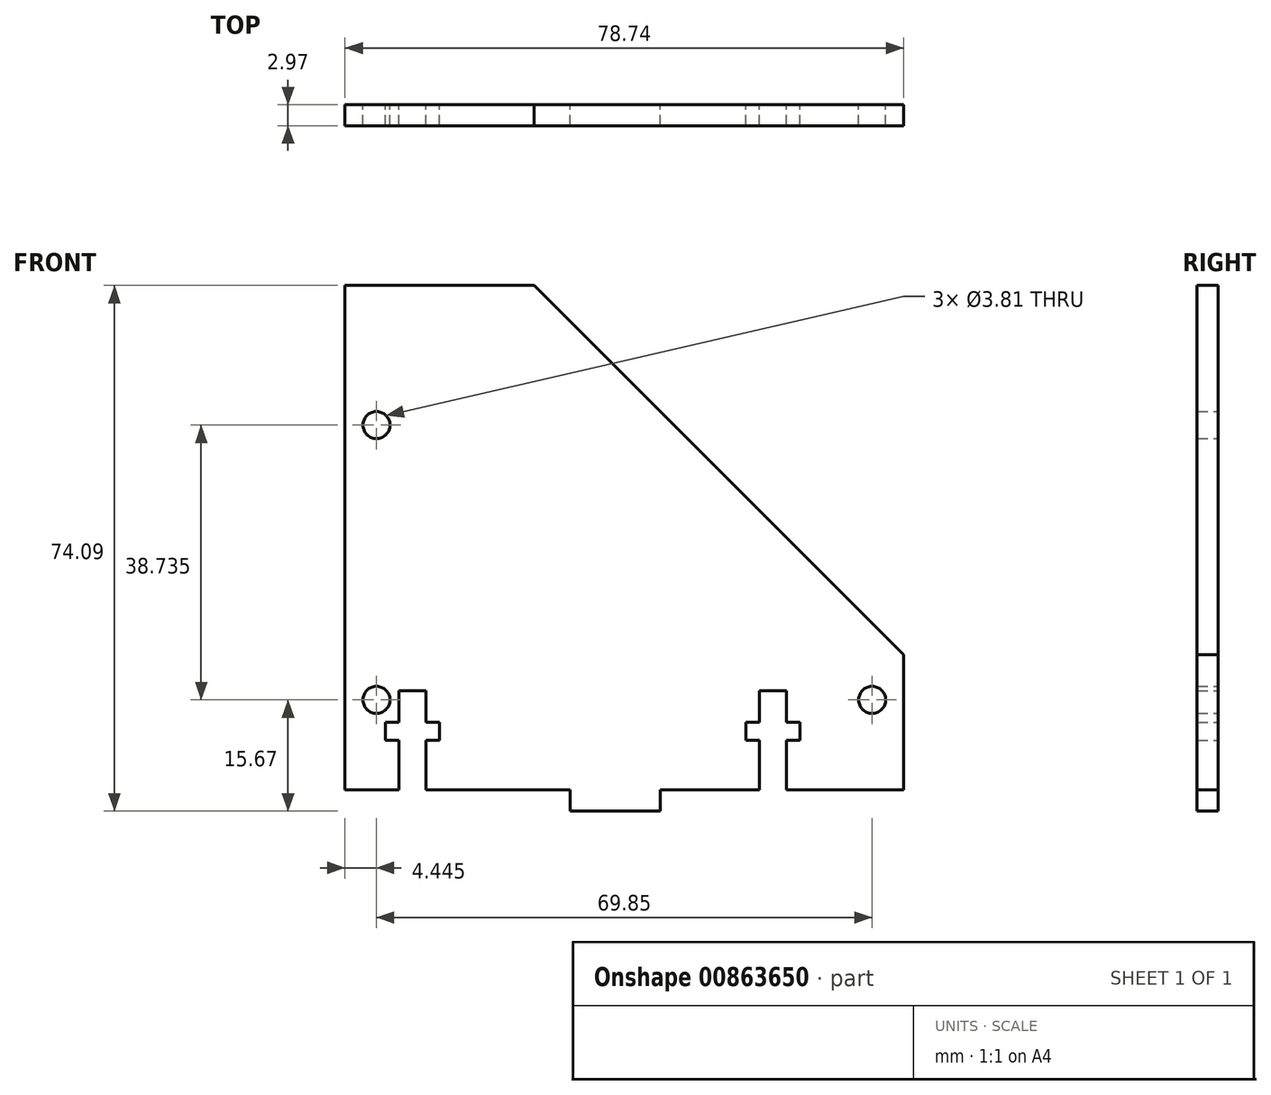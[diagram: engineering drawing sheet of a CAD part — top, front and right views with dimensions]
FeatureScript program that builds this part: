
annotation { "Feature Type Name" : "Feature", "Feature Type Description" : "" }
export const myFeature = defineFeature(function(context is Context, id is Id, definition is map)
    precondition{}
    {
        {
            var Q0;
            Q0=qCreatedBy(makeId("Front.planeOp"),FACE);
            var sketch = newSketch(context, id + "F0", { "sketchPlane" : qUnion([Q0])});
            skLineSegment(sketch, "E0", {"start": v(0, 0) * mm, "end": v(0, 71.12) * mm});
            skLineSegment(sketch, "E1", {"start": v(0, 71.12) * mm, "end": v(26.67, 71.12) * mm});
            skLineSegment(sketch, "E2", {"start": v(26.67, 71.12) * mm, "end": v(78.74, 19.05) * mm});
            skLineSegment(sketch, "E3", {"start": v(78.74, 19.05) * mm, "end": v(78.74, 0) * mm});
            skLineSegment(sketch, "E4", {"start": v(78.74, 0) * mm, "end": v(62.23, 0) * mm});
            skLineSegment(sketch, "E5", {"start": v(44.45, 0) * mm, "end": v(44.45, -2.97) * mm});
            skLineSegment(sketch, "E6", {"start": v(44.45, -2.97) * mm, "end": v(31.75, -2.97) * mm});
            skLineSegment(sketch, "E7", {"start": v(31.75, -2.97) * mm, "end": v(31.75, 0) * mm});
            skLineSegment(sketch, "E8", {"start": v(31.75, 0) * mm, "end": v(11.43, 0) * mm});
            skCircle(sketch, "E9", {"center": v(4.44, 51.44) * mm, "radius": 1.9 * mm});
            skCircle(sketch, "E10", {"center": v(4.45, 12.7) * mm, "radius": 1.9 * mm});
            skLineSegment(sketch, "E11", {"start": v(7.62, 0) * mm, "end": v(7.62, 6.99) * mm});
            skLineSegment(sketch, "E12", {"start": v(7.62, 6.99) * mm, "end": v(5.72, 6.99) * mm});
            skLineSegment(sketch, "E13", {"start": v(5.72, 6.99) * mm, "end": v(5.72, 9.53) * mm});
            skLineSegment(sketch, "E14", {"start": v(5.72, 9.53) * mm, "end": v(7.62, 9.53) * mm});
            skLineSegment(sketch, "E15", {"start": v(7.62, 9.53) * mm, "end": v(7.62, 13.97) * mm});
            skLineSegment(sketch, "E16", {"start": v(7.62, 13.97) * mm, "end": v(11.43, 13.97) * mm});
            skLineSegment(sketch, "E17", {"start": v(11.43, 13.97) * mm, "end": v(11.43, 9.53) * mm});
            skLineSegment(sketch, "E18", {"start": v(11.43, 9.53) * mm, "end": v(13.34, 9.53) * mm});
            skLineSegment(sketch, "E19", {"start": v(13.34, 9.53) * mm, "end": v(13.34, 6.99) * mm});
            skLineSegment(sketch, "E20", {"start": v(13.34, 6.99) * mm, "end": v(11.43, 6.99) * mm});
            skLineSegment(sketch, "E21", {"start": v(11.43, 6.99) * mm, "end": v(11.43, 0) * mm});
            skLineSegment(sketch, "E22.trimOffspring", {"start": v(7.62, 0) * mm, "end": v(0, 0) * mm});
            skCircle(sketch, "E23", {"center": v(74.3, 12.7) * mm, "radius": 1.9 * mm});
            skLineSegment(sketch, "E24", {"start": v(38.1, -2.97) * mm, "end": v(38.1, 59.69) * mm, "construction": true});
            skLineSegment(sketch, "E25.1.0.0", {"start": v(58.42, 0) * mm, "end": v(58.42, 6.99) * mm});
            skLineSegment(sketch, "E25.1.0.1", {"start": v(58.42, 6.99) * mm, "end": v(56.52, 6.99) * mm});
            skLineSegment(sketch, "E25.1.0.2", {"start": v(56.52, 6.99) * mm, "end": v(56.52, 9.53) * mm});
            skLineSegment(sketch, "E25.1.0.3", {"start": v(56.52, 9.53) * mm, "end": v(58.42, 9.53) * mm});
            skLineSegment(sketch, "E25.1.0.4", {"start": v(58.42, 9.53) * mm, "end": v(58.42, 13.97) * mm});
            skLineSegment(sketch, "E25.1.0.5", {"start": v(58.42, 13.97) * mm, "end": v(62.23, 13.97) * mm});
            skLineSegment(sketch, "E25.1.0.6", {"start": v(62.23, 13.97) * mm, "end": v(62.23, 9.53) * mm});
            skLineSegment(sketch, "E25.1.0.7", {"start": v(62.23, 9.53) * mm, "end": v(64.14, 9.53) * mm});
            skLineSegment(sketch, "E25.1.0.8", {"start": v(64.14, 6.99) * mm, "end": v(62.23, 6.99) * mm});
            skLineSegment(sketch, "E25.1.0.9", {"start": v(64.14, 9.53) * mm, "end": v(64.14, 6.99) * mm});
            skLineSegment(sketch, "E25.1.0.10", {"start": v(62.23, 6.99) * mm, "end": v(62.23, 0) * mm});
            skLineSegment(sketch, "E25.direction1", {"start": v(7.62, 0) * mm, "end": v(58.42, 0) * mm, "construction": true});
            skLineSegment(sketch, "E26.trimOffspring", {"start": v(58.42, 0) * mm, "end": v(44.45, 0) * mm});
            skSolve(sketch);
        }
        {
            var Q0;
            Q0 = qSketchRegion(id + "F0", true);
            extrude(context, id + "F1", {"entities" : qUnion([Q0]), "depth" : 2.97 * mm, "offsetDistance" : 25.4 * mm});
        }
    });
